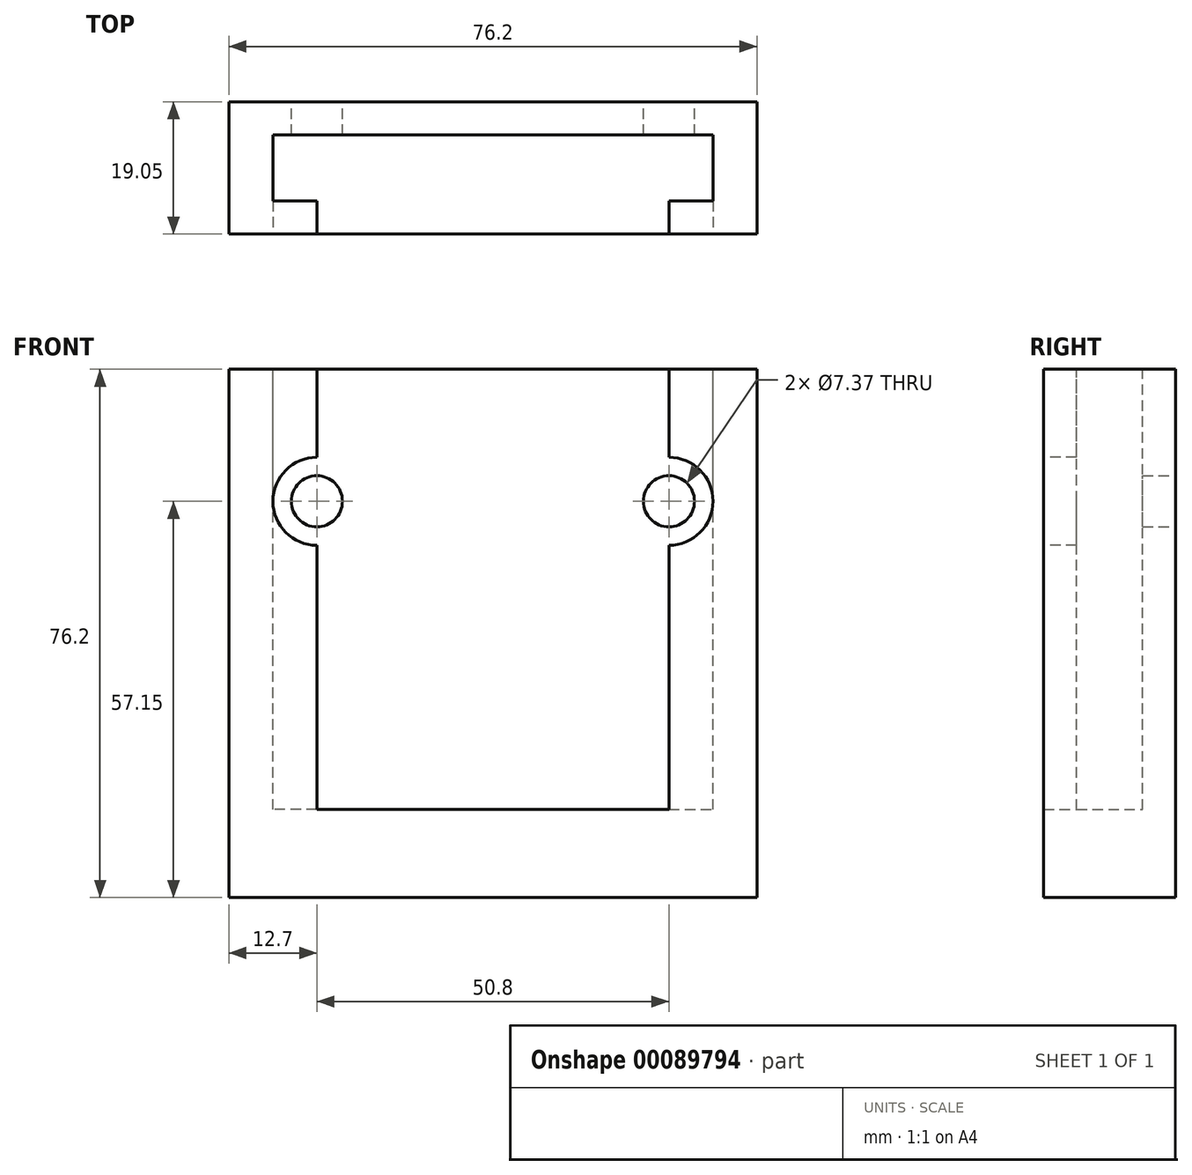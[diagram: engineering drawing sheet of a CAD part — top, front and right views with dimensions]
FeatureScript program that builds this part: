
annotation { "Feature Type Name" : "Feature", "Feature Type Description" : "" }
export const myFeature = defineFeature(function(context is Context, id is Id, definition is map)
    precondition{}
    {
        {
            var Q0;
            Q0=qCreatedBy(makeId("Front.planeOp"),FACE);
            var sketch = newSketch(context, id + "F0", { "sketchPlane" : qUnion([Q0])});
            skLineSegment(sketch, "E0", {"start": v(0, 0) * mm, "end": v(0, 38.1) * mm});
            skLineSegment(sketch, "E1", {"start": v(0, 0) * mm, "end": v(0, -38.1) * mm});
            skLineSegment(sketch, "E2", {"start": v(-38.1, 0) * mm, "end": v(-38.1, 38.1) * mm});
            skLineSegment(sketch, "E3", {"start": v(-38.1, 38.1) * mm, "end": v(38.1, 38.1) * mm});
            skLineSegment(sketch, "E4", {"start": v(38.1, 0) * mm, "end": v(38.1, 38.1) * mm});
            skLineSegment(sketch, "E5", {"start": v(38.1, 0) * mm, "end": v(38.1, -38.1) * mm});
            skLineSegment(sketch, "E6", {"start": v(38.1, -38.1) * mm, "end": v(-38.1, -38.1) * mm});
            skLineSegment(sketch, "E7", {"start": v(-38.1, 0) * mm, "end": v(-38.1, -38.1) * mm});
            skSolve(sketch);
        }
        {
            var Q0;
            Q0 = qSketchRegion(id + "F0", true);
            extrude(context, id + "F1", {"entities" : qUnion([Q0]), "depth" : 19.05 * mm});
        }
        {
            var Q0;
            Q0=makeQuery(id+"F1.opExtrude","SWEPT_FACE",FACE,{"disambiguationData":[OSD([sQuery(id+"F0.wireOp",EDGE,"E3")])]});
            var sketch = newSketch(context, id + "F2", { "sketchPlane" : qUnion([Q0])});
            skLineSegment(sketch, "E8", {"start": v(-38.1, -19.05) * mm, "end": v(-25.4, -19.05) * mm});
            skLineSegment(sketch, "E9", {"start": v(38.1, -19.05) * mm, "end": v(25.4, -19.05) * mm});
            skLineSegment(sketch, "E10", {"start": v(25.4, -19.05) * mm, "end": v(25.4, 0) * mm});
            skLineSegment(sketch, "E11", {"start": v(25.4, -9.53) * mm, "end": v(31.75, -9.53) * mm});
            skLineSegment(sketch, "E12", {"start": v(25.4, -9.53) * mm, "end": v(25.4, 0) * mm});
            skLineSegment(sketch, "E13", {"start": v(25.4, -4.76) * mm, "end": v(31.75, -4.76) * mm});
            skLineSegment(sketch, "E14", {"start": v(31.75, -4.76) * mm, "end": v(31.75, -9.53) * mm});
            skLineSegment(sketch, "E15", {"start": v(25.4, -9.53) * mm, "end": v(25.4, -19.05) * mm});
            skLineSegment(sketch, "E16", {"start": v(25.4, -14.29) * mm, "end": v(31.75, -14.29) * mm});
            skLineSegment(sketch, "E17", {"start": v(31.75, -14.29) * mm, "end": v(31.75, -9.53) * mm});
            skLineSegment(sketch, "E18.MirrorCS", {"start": v(-25.4, -19.05) * mm, "end": v(-25.4, 0) * mm});
            skLineSegment(sketch, "E19.MirrorCS", {"start": v(-25.4, -9.53) * mm, "end": v(-31.75, -9.53) * mm});
            skLineSegment(sketch, "E20.MirrorCS", {"start": v(-31.75, -14.29) * mm, "end": v(-31.75, -9.53) * mm});
            skLineSegment(sketch, "E21.MirrorCS", {"start": v(-25.4, -9.53) * mm, "end": v(-25.4, 0) * mm});
            skLineSegment(sketch, "E22.MirrorCS", {"start": v(-25.4, -4.76) * mm, "end": v(-31.75, -4.76) * mm});
            skLineSegment(sketch, "E23.MirrorCS", {"start": v(-25.4, -14.29) * mm, "end": v(-31.75, -14.29) * mm});
            skLineSegment(sketch, "E24.MirrorCS", {"start": v(-25.4, -9.53) * mm, "end": v(-25.4, -19.05) * mm});
            skLineSegment(sketch, "E25.MirrorCS", {"start": v(-31.75, -4.76) * mm, "end": v(-31.75, -9.53) * mm});
            skLineSegment(sketch, "E26", {"start": v(-31.75, -4.76) * mm, "end": v(31.75, -4.76) * mm});
            skLineSegment(sketch, "E27", {"start": v(31.75, -14.29) * mm, "end": v(-31.75, -14.29) * mm});
            skSolve(sketch);
        }
        {
            var Q0;
            Q0 = qSketchRegion(id + "F2", true);
            var Q1;
            {var subQ0=sQuery(id+"F2.wireOp",EDGE,"E15");var subQ3=sQuery(id+"F2.wireOp",EDGE,"E27");var subQ4=makeQuery(id+"F2.imprint","INTERSECT",VERTEX,{"derivedFrom":[subQ0,subQ3]});Q1=makeQuery(id+"F2.imprint","IMPRINT",FACE,{"disambiguationData":[TD([[makeQuery(id+"F2.imprint","IMPRINT",EDGE,{"disambiguationData":[TD([[subQ4,-1.0]])],"derivedFrom":subQ3}),1.0]])]});}
            extrude(context, id + "F3", {"entities" : qUnion([Q0, Q1]), "operationType" : NewBodyOperationType.REMOVE, "oppositeDirection" : true, "depth" : 63.5 * mm});
        }
        {
            var Q0;
            Q0=makeQuery(id+"F1.opExtrude","CAP_FACE",FACE,{"disambiguationData":[OSD([sQuery(id+"F0.wireOp",EDGE,"E2"),sQuery(id+"F0.wireOp",EDGE,"E3"),sQuery(id+"F0.wireOp",EDGE,"E4"),sQuery(id+"F0.wireOp",EDGE,"E5"),sQuery(id+"F0.wireOp",EDGE,"E6"),sQuery(id+"F0.wireOp",EDGE,"E7")])],"isStart":true});
            var sketch = newSketch(context, id + "F4", { "sketchPlane" : qUnion([Q0])});
            skLineSegment(sketch, "E28", {"start": v(0, 0) * mm, "end": v(0, 38.1) * mm});
            skLineSegment(sketch, "E29", {"start": v(0, 38.1) * mm, "end": v(0, 19.05) * mm});
            skLineSegment(sketch, "E30", {"start": v(0, 19.05) * mm, "end": v(-38.1, 19.05) * mm});
            skLineSegment(sketch, "E31", {"start": v(0, 19.05) * mm, "end": v(38.1, 19.05) * mm});
            skLineSegment(sketch, "E32", {"start": v(38.1, 19.05) * mm, "end": v(25.4, 19.05) * mm});
            skLineSegment(sketch, "E33", {"start": v(-38.1, 19.05) * mm, "end": v(-25.4, 19.05) * mm});
            skCircle(sketch, "E34", {"center": v(-25.4, 19.05) * mm, "radius": 3.68 * mm});
            skCircle(sketch, "E35", {"center": v(25.4, 19.05) * mm, "radius": 3.68 * mm});
            skSolve(sketch);
        }
        {
            var Q0;
            Q0 = qSketchRegion(id + "F4", true);
            extrude(context, id + "F5", {"entities" : qUnion([Q0]), "operationType" : NewBodyOperationType.REMOVE, "oppositeDirection" : true, "depth" : 10.16 * mm});
        }
        {
            var Q0;
            Q0=makeQuery(id+"F3.boolean.opBoolean","COPY",FACE,{"derivedFrom":makeQuery(id+"F3.opExtrude","SWEPT_FACE",FACE,{"disambiguationData":[OSD([sQuery(id+"F2.wireOp",EDGE,"E26")])]})});
            var sketch = newSketch(context, id + "F6", { "sketchPlane" : qUnion([Q0])});
            skLineSegment(sketch, "E36", {"start": v(25.4, 19.05) * mm, "end": v(19.84, 19.05) * mm});
            skLineSegment(sketch, "E37", {"start": v(25.4, 19.05) * mm, "end": v(30.96, 19.05) * mm});
            skSolve(sketch);
        }
        {
            var Q0;
            Q0=makeQuery(id+"F1.opExtrude","CAP_FACE",FACE,{"disambiguationData":[OSD([sQuery(id+"F0.wireOp",EDGE,"E2"),sQuery(id+"F0.wireOp",EDGE,"E3"),sQuery(id+"F0.wireOp",EDGE,"E4"),sQuery(id+"F0.wireOp",EDGE,"E5"),sQuery(id+"F0.wireOp",EDGE,"E6"),sQuery(id+"F0.wireOp",EDGE,"E7")])],"isStart":false});
            var sketch = newSketch(context, id + "F7", { "sketchPlane" : qUnion([Q0])});
            skLineSegment(sketch, "E38", {"start": v(-25.4, 38.1) * mm, "end": v(-38.1, 38.1) * mm});
            skLineSegment(sketch, "E39", {"start": v(-38.1, 38.1) * mm, "end": v(-25.4, 38.1) * mm});
            skLineSegment(sketch, "E40", {"start": v(-25.4, 19.04) * mm, "end": v(-25.4, 38.1) * mm});
            skCircle(sketch, "E41", {"center": v(-25.4, 19.04) * mm, "radius": 6.35 * mm});
            skLineSegment(sketch, "E42", {"start": v(25.4, 38.1) * mm, "end": v(25.4, 19.05) * mm});
            skCircle(sketch, "E43", {"center": v(25.4, 19.05) * mm, "radius": 6.35 * mm});
            skSolve(sketch);
        }
        {
            var Q0;
            Q0 = qSketchRegion(id + "F7", true);
            extrude(context, id + "F8", {"entities" : qUnion([Q0]), "operationType" : NewBodyOperationType.REMOVE, "oppositeDirection" : true, "depth" : 12.7 * mm});
        }
    });
